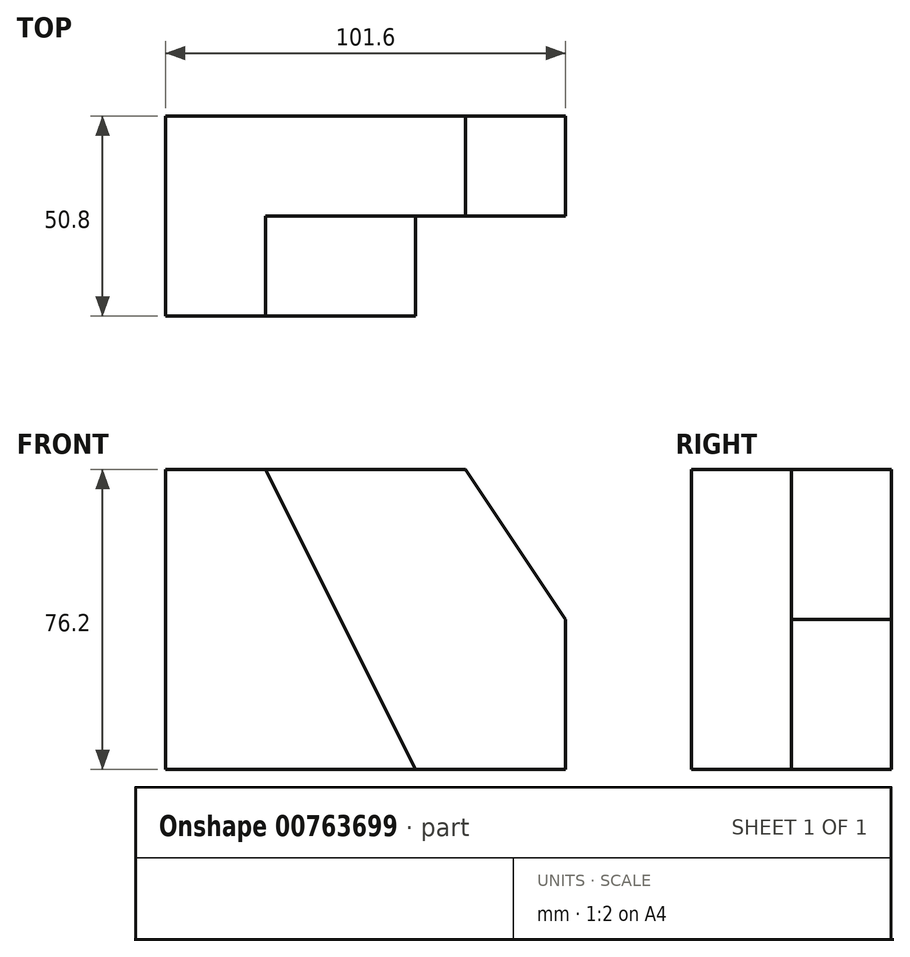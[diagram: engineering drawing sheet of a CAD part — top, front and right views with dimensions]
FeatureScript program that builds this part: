
annotation { "Feature Type Name" : "Feature", "Feature Type Description" : "" }
export const myFeature = defineFeature(function(context is Context, id is Id, definition is map)
    precondition{}
    {
        {
            var Q0;
            Q0=qCreatedBy(makeId("Front.planeOp"),FACE);
            var sketch = newSketch(context, id + "F0", { "sketchPlane" : qUnion([Q0])});
            skLineSegment(sketch, "E0.bottom", {"start": v(50.8, -38.1) * mm, "end": v(-50.8, -38.1) * mm});
            skLineSegment(sketch, "E0.top", {"start": v(50.8, 38.1) * mm, "end": v(-50.8, 38.1) * mm});
            skLineSegment(sketch, "E0.left", {"start": v(50.8, -38.1) * mm, "end": v(50.8, 38.1) * mm});
            skLineSegment(sketch, "E0.right", {"start": v(-50.8, -38.1) * mm, "end": v(-50.8, 38.1) * mm});
            skPoint(sketch, "E0.middle", {"position": v(0, 0) * mm});
            skSolve(sketch);
        }
        {
            var Q0;
            Q0 = qSketchRegion(id + "F0", true);
            extrude(context, id + "F1", {"entities" : qUnion([Q0]), "depth" : 50.8 * mm, "offsetDistance" : 25.4 * mm});
        }
        {
            var Q0;
            Q0=makeQuery(id+"F1.opExtrude","CAP_FACE",FACE,{"disambiguationData":[OSD([sQuery(id+"F0.wireOp",EDGE,"E0.bottom"),sQuery(id+"F0.wireOp",EDGE,"E0.top"),sQuery(id+"F0.wireOp",EDGE,"E0.left"),sQuery(id+"F0.wireOp",EDGE,"E0.right")])],"isStart":false});
            var sketch = newSketch(context, id + "F2", { "sketchPlane" : qUnion([Q0])});
            skLineSegment(sketch, "E1", {"start": v(-25.4, 38.1) * mm, "end": v(12.7, -38.1) * mm});
            skLineSegment(sketch, "E2", {"start": v(12.7, -38.1) * mm, "end": v(50.8, -38.1) * mm});
            skLineSegment(sketch, "E3", {"start": v(50.8, -38.1) * mm, "end": v(50.8, 38.1) * mm});
            skLineSegment(sketch, "E4", {"start": v(50.8, 38.1) * mm, "end": v(-25.4, 38.1) * mm});
            skSolve(sketch);
        }
        {
            var Q0;
            Q0 = qSketchRegion(id + "F2", true);
            extrude(context, id + "F3", {"entities" : qUnion([Q0]), "operationType" : NewBodyOperationType.REMOVE, "oppositeDirection" : true, "depth" : 25.4 * mm, "offsetDistance" : 25.4 * mm});
        }
        {
            var Q0;
            Q0=makeQuery(id+"F3.boolean.opBoolean","COPY",FACE,{"derivedFrom":makeQuery(id+"F3.opExtrude","CAP_FACE",FACE,{"disambiguationData":[OSD([sQuery(id+"F2.wireOp",EDGE,"E1"),sQuery(id+"F2.wireOp",EDGE,"E2"),sQuery(id+"F2.wireOp",EDGE,"E3"),sQuery(id+"F2.wireOp",EDGE,"E4")])],"isStart":false})});
            var sketch = newSketch(context, id + "F4", { "sketchPlane" : qUnion([Q0])});
            skLineSegment(sketch, "E5", {"start": v(25.4, 38.1) * mm, "end": v(50.8, 0) * mm});
            skLineSegment(sketch, "E6", {"start": v(50.8, 0) * mm, "end": v(50.8, 38.1) * mm});
            skLineSegment(sketch, "E7", {"start": v(50.8, 38.1) * mm, "end": v(25.4, 38.1) * mm});
            skSolve(sketch);
        }
        {
            var Q0;
            Q0 = qSketchRegion(id + "F4", true);
            extrude(context, id + "F5", {"entities" : qUnion([Q0]), "operationType" : NewBodyOperationType.REMOVE, "oppositeDirection" : true, "depth" : 25.4 * mm, "offsetDistance" : 25.4 * mm});
        }
    });
